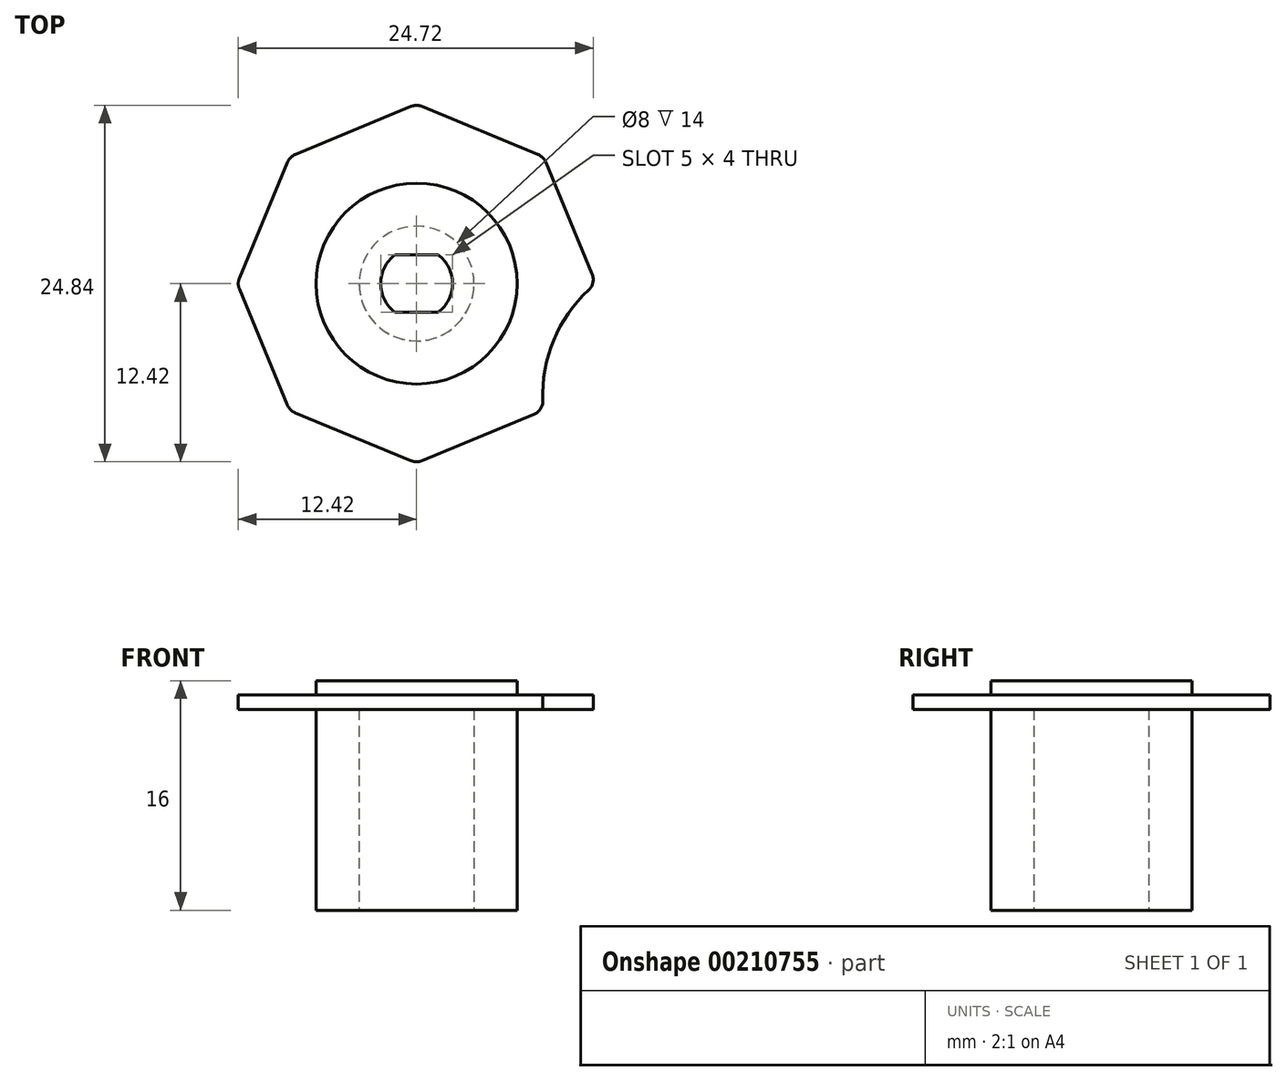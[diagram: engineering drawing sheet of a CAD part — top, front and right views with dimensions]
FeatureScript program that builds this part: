
annotation { "Feature Type Name" : "Feature", "Feature Type Description" : "" }
export const myFeature = defineFeature(function(context is Context, id is Id, definition is map)
    precondition{}
    {
        {
            var Q0;
            Q0=qCreatedBy(makeId("Top.planeOp"),FACE);
            var sketch = newSketch(context, id + "F0", { "sketchPlane" : qUnion([Q0])});
            skCircle(sketch, "E0", {"center": v(0, 0) * mm, "radius": 7 * mm});
            skSolve(sketch);
        }
        {
            var Q0;
            Q0 = qSketchRegion(id + "F0", true);
            extrude(context, id + "F1", {"entities" : qUnion([Q0]), "depth" : 16 * mm});
        }
        {
            var Q0;
            Q0=makeQuery(id+"F1.opExtrude","CAP_FACE",FACE,{"disambiguationData":[OSD([sQuery(id+"F0.wireOp",EDGE,"E0")])],"isStart":false});
            cPlane(context, id + "F2", {"entities" : qUnion([Q0]), "cplaneType" : CPlaneType.OFFSET, "offset" : 1 * mm, "oppositeDirection" : true, "width" : 150 * mm, "height" : 150 * mm});
        }
        {
            var Q0;
            Q0=qCreatedBy(id+"F2.planeOp",FACE);
            var sketch = newSketch(context, id + "F3", { "sketchPlane" : qUnion([Q0])});
            skCircle(sketch, "E1.cCircle", {"center": v(0, 0) * mm, "radius": 12.5 * mm, "construction": true});
            skLineSegment(sketch, "E1.0", {"start": v(0, 12.5) * mm, "end": v(8.84, 8.84) * mm});
            skLineSegment(sketch, "E1.1", {"start": v(8.84, 8.84) * mm, "end": v(12.5, 0) * mm});
            skLineSegment(sketch, "E1.2", {"start": v(12.5, 0) * mm, "end": v(8.84, -8.84) * mm});
            skLineSegment(sketch, "E1.3", {"start": v(8.84, -8.84) * mm, "end": v(0, -12.5) * mm});
            skLineSegment(sketch, "E1.4", {"start": v(0, -12.5) * mm, "end": v(-8.84, -8.84) * mm});
            skLineSegment(sketch, "E1.5", {"start": v(-8.84, -8.84) * mm, "end": v(-12.5, 0) * mm});
            skLineSegment(sketch, "E1.6", {"start": v(-12.5, 0) * mm, "end": v(-8.84, 8.84) * mm});
            skLineSegment(sketch, "E1.7", {"start": v(-8.84, 8.84) * mm, "end": v(0, 12.5) * mm});
            skSolve(sketch);
        }
        {
            var Q0;
            Q0 = qSketchRegion(id + "F3", true);
            extrude(context, id + "F4", {"entities" : qUnion([Q0]), "operationType" : NewBodyOperationType.ADD, "oppositeDirection" : true, "depth" : 1 * mm});
        }
        {
            var Q0;
            Q0=makeQuery(id+"F4.opExtrude","CAP_FACE",FACE,{"disambiguationData":[OSD([sQuery(id+"F3.wireOp",EDGE,"E1.0"),sQuery(id+"F3.wireOp",EDGE,"E1.1"),sQuery(id+"F3.wireOp",EDGE,"E1.2"),sQuery(id+"F3.wireOp",EDGE,"E1.3"),sQuery(id+"F3.wireOp",EDGE,"E1.4"),sQuery(id+"F3.wireOp",EDGE,"E1.5"),sQuery(id+"F3.wireOp",EDGE,"E1.6"),sQuery(id+"F3.wireOp",EDGE,"E1.7")])],"isStart":true});
            var sketch = newSketch(context, id + "F5", { "sketchPlane" : qUnion([Q0])});
            skCircle(sketch, "E2", {"center": v(18.78, -7.78) * mm, "radius": 10 * mm});
            skPoint(sketch, "E2.first.point", {"position": v(12.5, 0) * mm});
            skPoint(sketch, "E2.second.point", {"position": v(8.84, -8.84) * mm});
            skPoint(sketch, "E2.third.point", {"position": v(25.55, -15.15) * mm});
            skSolve(sketch);
        }
        {
            var Q0;
            {var subQ1=makeQuery(id+"F4.opExtrude","CAP_EDGE",EDGE,{"disambiguationData":[OSD([sQuery(id+"F3.wireOp",EDGE,"E1.2")])],"isStart":true});Q0=makeQuery(id+"F5.imprint","IMPRINT",FACE,{"disambiguationData":[TD([[makeQuery(id+"F5.imprint","IMPRINT",EDGE,{"derivedFrom":subQ1}),-1.0]])]});}
            extrude(context, id + "F6", {"entities" : qUnion([Q0]), "operationType" : NewBodyOperationType.REMOVE, "endBound" : BoundingType.UP_TO_NEXT, "oppositeDirection" : true, "depth" : 25 * mm});
        }
        {
            var Q0;
            Q0=makeQuery(id+"F1.opExtrude","CAP_FACE",FACE,{"disambiguationData":[OSD([sQuery(id+"F0.wireOp",EDGE,"E0")])],"isStart":false});
            cPlane(context, id + "F7", {"entities" : qUnion([Q0]), "cplaneType" : CPlaneType.OFFSET, "offset" : 2 * mm, "oppositeDirection" : true, "width" : 150 * mm, "height" : 150 * mm});
        }
        {
            var Q0;
            Q0=makeQuery(id+"F1.opExtrude","CAP_FACE",FACE,{"disambiguationData":[OSD([sQuery(id+"F0.wireOp",EDGE,"E0")])],"isStart":true});
            var sketch = newSketch(context, id + "F8", { "sketchPlane" : qUnion([Q0])});
            skCircle(sketch, "E3", {"center": v(0, 0) * mm, "radius": 4 * mm});
            skSolve(sketch);
        }
        {
            var Q0;
            Q0 = qSketchRegion(id + "F8", true);
            var Q1;
            Q1=qCreatedBy(id+"F7.planeOp",FACE);
            extrude(context, id + "F9", {"entities" : qUnion([Q0]), "operationType" : NewBodyOperationType.REMOVE, "endBound" : BoundingType.UP_TO_SURFACE, "oppositeDirection" : true, "endBoundEntityFace" : qUnion([Q1]), "depth" : 25 * mm});
        }
        {
            var Q0;
            Q0=makeQuery(id+"F1.opExtrude","CAP_FACE",FACE,{"disambiguationData":[OSD([sQuery(id+"F0.wireOp",EDGE,"E0")])],"isStart":false});
            var sketch = newSketch(context, id + "F10", { "sketchPlane" : qUnion([Q0])});
            skCircle(sketch, "E4", {"center": v(0, 0) * mm, "radius": 2.5 * mm});
            skLineSegment(sketch, "E5", {"start": v(-1.5, 2) * mm, "end": v(1.5, 2) * mm});
            skLineSegment(sketch, "E6", {"start": v(-1.5, -2) * mm, "end": v(1.5, -2) * mm});
            skSolve(sketch);
        }
        {
            var Q0;
            {var subQ0=sQuery(id+"F10.wireOp",EDGE,"E5");Q0=makeQuery(id+"F10.imprint","IMPRINT",FACE,{"disambiguationData":[TD([[makeQuery(id+"F10.imprint","IMPRINT",EDGE,{"derivedFrom":subQ0}),-1.0]])]});}
            extrude(context, id + "F11", {"entities" : qUnion([Q0]), "operationType" : NewBodyOperationType.REMOVE, "endBound" : BoundingType.UP_TO_NEXT, "oppositeDirection" : true, "depth" : 25 * mm});
        }
        {
            var Q0;
            {var subQ0=sQuery(id+"F5.wireOp",EDGE,"E2");var subQ1=sQuery(id+"F3.wireOp",EDGE,"E1.2");var subQ2=sQuery(id+"F3.wireOp",EDGE,"E1.1");Q0=makeQuery(id+"Fe7eZynt9cMowC5_1.1.F6.boolean.opBoolean","MERGE",EDGE,{"derivedFrom":[makeQuery(id+"F6.boolean.opBoolean","MERGE",EDGE,{"derivedFrom":[makeQuery(id+"F4.opExtrude","SWEPT_EDGE",EDGE,{"disambiguationData":[OSD([subQ2,subQ1])]}),makeQuery(id+"F6.opExtrude","SWEPT_EDGE",EDGE,{"disambiguationData":[OSD([subQ2,subQ1,subQ0])]})]}),makeQuery(id+"Fe7eZynt9cMowC5_1.1.F6.opExtrude","SWEPT_EDGE",EDGE,{"disambiguationData":[OSD([subQ2,subQ1,sQuery(id+"F3.wireOp",EDGE,"E1.3"),subQ0])]})]});}
            var Q1;
            {var subQ0=sQuery(id+"F5.wireOp",EDGE,"E2");var subQ1=sQuery(id+"F3.wireOp",EDGE,"E1.3");var subQ2=sQuery(id+"F3.wireOp",EDGE,"E1.2");Q1=makeQuery(id+"Fe7eZynt9cMowC5_1.7.F6.boolean.opBoolean","MERGE",EDGE,{"derivedFrom":[makeQuery(id+"F6.boolean.opBoolean","MERGE",EDGE,{"derivedFrom":[makeQuery(id+"F4.opExtrude","SWEPT_EDGE",EDGE,{"disambiguationData":[OSD([subQ2,subQ1])]}),makeQuery(id+"F6.opExtrude","SWEPT_EDGE",EDGE,{"disambiguationData":[OSD([subQ2,subQ1,subQ0])]})]}),makeQuery(id+"Fe7eZynt9cMowC5_1.7.F6.opExtrude","SWEPT_EDGE",EDGE,{"disambiguationData":[OSD([sQuery(id+"F3.wireOp",EDGE,"E1.1"),subQ2,subQ1,subQ0])]})]});}
            var Q2;
            {var subQ0=sQuery(id+"F5.wireOp",EDGE,"E2");var subQ1=sQuery(id+"F3.wireOp",EDGE,"E1.4");var subQ2=sQuery(id+"F3.wireOp",EDGE,"E1.3");var subQ3=sQuery(id+"F3.wireOp",EDGE,"E1.2");var subQ4=sQuery(id+"F3.wireOp",EDGE,"E1.1");Q2=makeQuery(id+"Fe7eZynt9cMowC5_1.7.F6.boolean.opBoolean","MERGE",EDGE,{"derivedFrom":[makeQuery(id+"Fe7eZynt9cMowC5_1.6.F6.boolean.opBoolean","MERGE",EDGE,{"derivedFrom":[makeQuery(id+"F4.opExtrude","SWEPT_EDGE",EDGE,{"disambiguationData":[OSD([subQ2,subQ1])]}),makeQuery(id+"Fe7eZynt9cMowC5_1.6.F6.opExtrude","SWEPT_EDGE",EDGE,{"disambiguationData":[OSD([subQ4,subQ3,subQ2,subQ1,subQ0])]})]}),makeQuery(id+"Fe7eZynt9cMowC5_1.7.F6.opExtrude","SWEPT_EDGE",EDGE,{"disambiguationData":[OSD([subQ4,subQ3,subQ2,subQ1,subQ0])]})]});}
            var Q3;
            {var subQ0=sQuery(id+"F5.wireOp",EDGE,"E2");var subQ1=sQuery(id+"F3.wireOp",EDGE,"E1.5");var subQ2=sQuery(id+"F3.wireOp",EDGE,"E1.4");var subQ3=sQuery(id+"F3.wireOp",EDGE,"E1.2");var subQ4=sQuery(id+"F3.wireOp",EDGE,"E1.1");Q3=makeQuery(id+"Fe7eZynt9cMowC5_1.6.F6.boolean.opBoolean","MERGE",EDGE,{"derivedFrom":[makeQuery(id+"Fe7eZynt9cMowC5_1.5.F6.boolean.opBoolean","MERGE",EDGE,{"derivedFrom":[makeQuery(id+"F4.opExtrude","SWEPT_EDGE",EDGE,{"disambiguationData":[OSD([subQ2,subQ1])]}),makeQuery(id+"Fe7eZynt9cMowC5_1.5.F6.opExtrude","SWEPT_EDGE",EDGE,{"disambiguationData":[OSD([subQ4,subQ3,subQ2,subQ1,subQ0])]})]}),makeQuery(id+"Fe7eZynt9cMowC5_1.6.F6.opExtrude","SWEPT_EDGE",EDGE,{"disambiguationData":[OSD([subQ4,subQ3,sQuery(id+"F3.wireOp",EDGE,"E1.3"),subQ2,subQ1,subQ0])]})]});}
            var Q4;
            {var subQ0=sQuery(id+"F5.wireOp",EDGE,"E2");var subQ1=sQuery(id+"F3.wireOp",EDGE,"E1.2");var subQ2=sQuery(id+"F3.wireOp",EDGE,"E1.1");var subQ3=sQuery(id+"F3.wireOp",EDGE,"E1.0");Q4=makeQuery(id+"Fe7eZynt9cMowC5_1.2.F6.boolean.opBoolean","MERGE",EDGE,{"derivedFrom":[makeQuery(id+"Fe7eZynt9cMowC5_1.1.F6.boolean.opBoolean","MERGE",EDGE,{"derivedFrom":[makeQuery(id+"F4.opExtrude","SWEPT_EDGE",EDGE,{"disambiguationData":[OSD([subQ3,subQ2])]}),makeQuery(id+"Fe7eZynt9cMowC5_1.1.F6.opExtrude","SWEPT_EDGE",EDGE,{"disambiguationData":[OSD([subQ3,subQ2,subQ1,subQ0])]})]}),makeQuery(id+"Fe7eZynt9cMowC5_1.2.F6.opExtrude","SWEPT_EDGE",EDGE,{"disambiguationData":[OSD([subQ3,subQ2,subQ1,sQuery(id+"F3.wireOp",EDGE,"E1.3"),subQ0])]})]});}
            var Q5;
            {var subQ0=sQuery(id+"F5.wireOp",EDGE,"E2");var subQ1=sQuery(id+"F3.wireOp",EDGE,"E1.7");var subQ2=sQuery(id+"F3.wireOp",EDGE,"E1.2");var subQ3=sQuery(id+"F3.wireOp",EDGE,"E1.1");var subQ4=sQuery(id+"F3.wireOp",EDGE,"E1.0");Q5=makeQuery(id+"Fe7eZynt9cMowC5_1.3.F6.boolean.opBoolean","MERGE",EDGE,{"derivedFrom":[makeQuery(id+"Fe7eZynt9cMowC5_1.2.F6.boolean.opBoolean","MERGE",EDGE,{"derivedFrom":[makeQuery(id+"F4.opExtrude","SWEPT_EDGE",EDGE,{"disambiguationData":[OSD([subQ4,subQ1])]}),makeQuery(id+"Fe7eZynt9cMowC5_1.2.F6.opExtrude","SWEPT_EDGE",EDGE,{"disambiguationData":[OSD([subQ4,subQ3,subQ2,subQ1,subQ0])]})]}),makeQuery(id+"Fe7eZynt9cMowC5_1.3.F6.opExtrude","SWEPT_EDGE",EDGE,{"disambiguationData":[OSD([subQ4,subQ3,subQ2,sQuery(id+"F3.wireOp",EDGE,"E1.3"),subQ1,subQ0])]})]});}
            var Q6;
            {var subQ0=sQuery(id+"F5.wireOp",EDGE,"E2");var subQ1=sQuery(id+"F3.wireOp",EDGE,"E1.7");var subQ2=sQuery(id+"F3.wireOp",EDGE,"E1.6");var subQ3=sQuery(id+"F3.wireOp",EDGE,"E1.2");var subQ4=sQuery(id+"F3.wireOp",EDGE,"E1.1");Q6=makeQuery(id+"Fe7eZynt9cMowC5_1.4.F6.boolean.opBoolean","MERGE",EDGE,{"derivedFrom":[makeQuery(id+"Fe7eZynt9cMowC5_1.3.F6.boolean.opBoolean","MERGE",EDGE,{"derivedFrom":[makeQuery(id+"F4.opExtrude","SWEPT_EDGE",EDGE,{"disambiguationData":[OSD([subQ2,subQ1])]}),makeQuery(id+"Fe7eZynt9cMowC5_1.3.F6.opExtrude","SWEPT_EDGE",EDGE,{"disambiguationData":[OSD([subQ4,subQ3,subQ2,subQ1,subQ0])]})]}),makeQuery(id+"Fe7eZynt9cMowC5_1.4.F6.opExtrude","SWEPT_EDGE",EDGE,{"disambiguationData":[OSD([subQ4,subQ3,sQuery(id+"F3.wireOp",EDGE,"E1.3"),subQ2,subQ1,subQ0])]})]});}
            var Q7;
            {var subQ0=sQuery(id+"F5.wireOp",EDGE,"E2");var subQ1=sQuery(id+"F3.wireOp",EDGE,"E1.6");var subQ2=sQuery(id+"F3.wireOp",EDGE,"E1.5");var subQ3=sQuery(id+"F3.wireOp",EDGE,"E1.2");var subQ4=sQuery(id+"F3.wireOp",EDGE,"E1.1");Q7=makeQuery(id+"Fe7eZynt9cMowC5_1.5.F6.boolean.opBoolean","MERGE",EDGE,{"derivedFrom":[makeQuery(id+"Fe7eZynt9cMowC5_1.4.F6.boolean.opBoolean","MERGE",EDGE,{"derivedFrom":[makeQuery(id+"F4.opExtrude","SWEPT_EDGE",EDGE,{"disambiguationData":[OSD([subQ2,subQ1])]}),makeQuery(id+"Fe7eZynt9cMowC5_1.4.F6.opExtrude","SWEPT_EDGE",EDGE,{"disambiguationData":[OSD([subQ4,subQ3,subQ2,subQ1,subQ0])]})]}),makeQuery(id+"Fe7eZynt9cMowC5_1.5.F6.opExtrude","SWEPT_EDGE",EDGE,{"disambiguationData":[OSD([subQ4,subQ3,sQuery(id+"F3.wireOp",EDGE,"E1.3"),subQ2,subQ1,subQ0])]})]});}
            fillet(context, id + "F12", {"entities" : qUnion([Q0, Q1, Q2, Q3, Q4, Q5, Q6, Q7]), "radius" : 1 * mm, "tangentPropagation" : true, "allowEdgeOverflow" : false});
        }
    });
